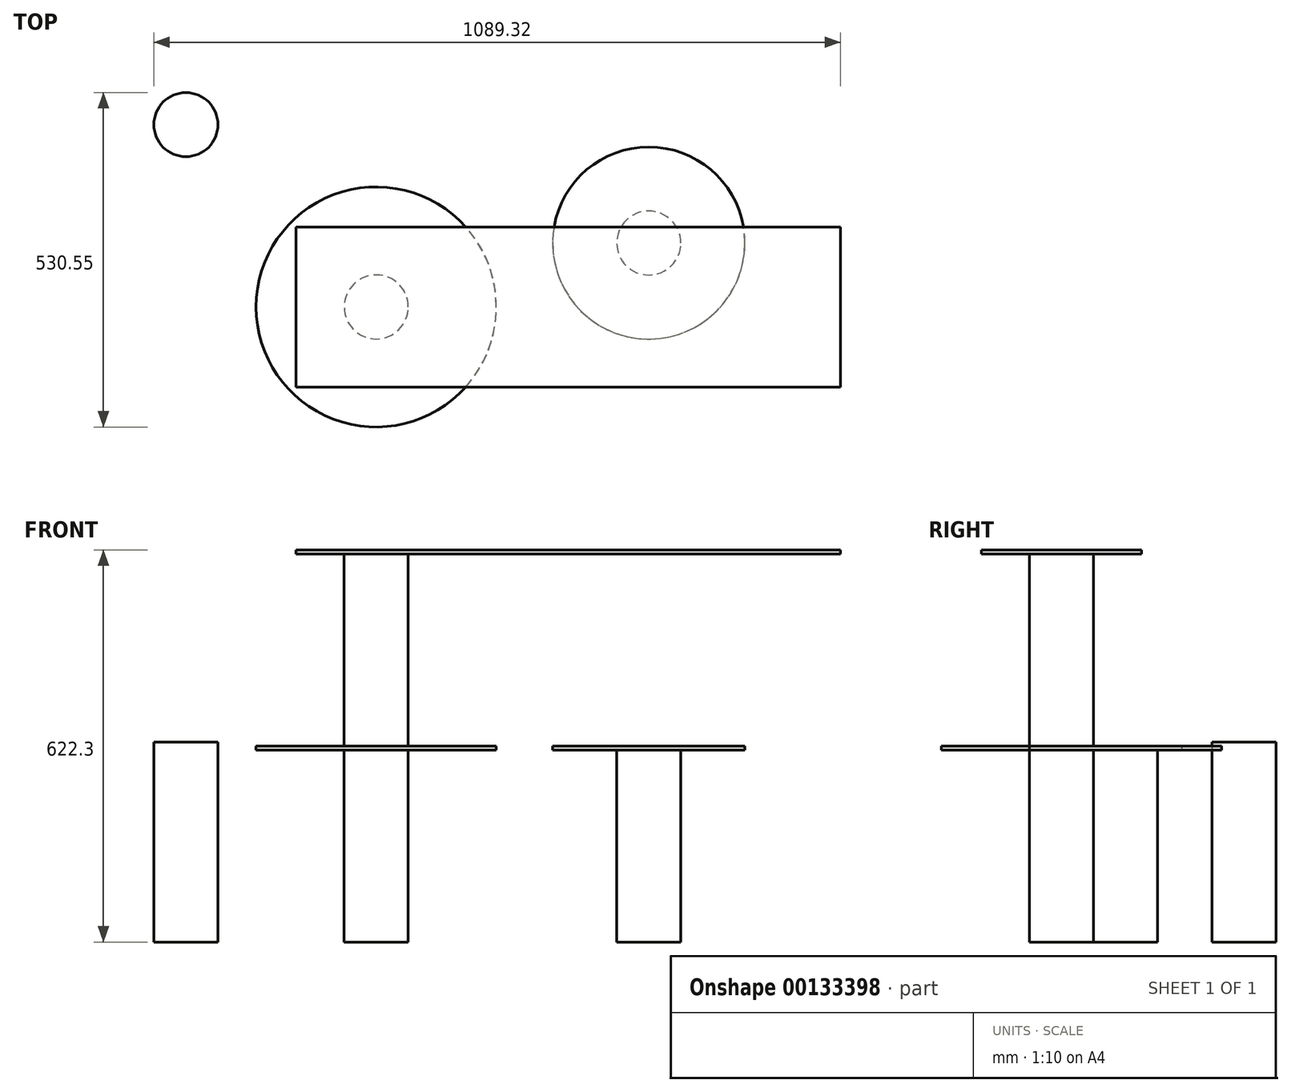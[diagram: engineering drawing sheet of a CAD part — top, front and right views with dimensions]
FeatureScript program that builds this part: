
annotation { "Feature Type Name" : "Feature", "Feature Type Description" : "" }
export const myFeature = defineFeature(function(context is Context, id is Id, definition is map)
    precondition{}
    {
        {
            var Q0;
            Q0=qCreatedBy(makeId("Top.planeOp"),FACE);
            var sketch = newSketch(context, id + "F0", { "sketchPlane" : qUnion([Q0])});
            skCircle(sketch, "E0", {"center": v(0, 0) * mm, "radius": 50.8 * mm});
            skSolve(sketch);
        }
        {
            var Q0;
            Q0 = qSketchRegion(id + "F0", true);
            extrude(context, id + "F1", {"entities" : qUnion([Q0]), "depth" : 304.8 * mm});
        }
        {
            var Q0;
            Q0=makeQuery(id+"F1.opExtrude","CAP_FACE",FACE,{"disambiguationData":[OSD([sQuery(id+"F0.wireOp",EDGE,"E0")])],"isStart":false});
            var sketch = newSketch(context, id + "F2", { "sketchPlane" : qUnion([Q0])});
            skCircle(sketch, "E1", {"center": v(0, 0) * mm, "radius": 152.4 * mm});
            skSolve(sketch);
        }
        {
            var Q0;
            Q0 = qSketchRegion(id + "F2", true);
            extrude(context, id + "F3", {"entities" : qUnion([Q0]), "operationType" : NewBodyOperationType.ADD, "depth" : 6.35 * mm});
        }
        {
            var Q0;
            Q0=qCreatedBy(makeId("Top.planeOp"),FACE);
            var sketch = newSketch(context, id + "F4", { "sketchPlane" : qUnion([Q0])});
            skCircle(sketch, "E2", {"center": v(-432.24, -101.35) * mm, "radius": 50.8 * mm});
            skSolve(sketch);
        }
        {
            var Q0;
            Q0 = qSketchRegion(id + "F4", true);
            extrude(context, id + "F5", {"entities" : qUnion([Q0]), "depth" : 304.8 * mm});
        }
        {
            var Q0;
            Q0=makeQuery(id+"F5.opExtrude","CAP_FACE",FACE,{"disambiguationData":[OSD([sQuery(id+"F4.wireOp",EDGE,"E2")])],"isStart":false});
            var sketch = newSketch(context, id + "F6", { "sketchPlane" : qUnion([Q0])});
            skCircle(sketch, "E3", {"center": v(-432.24, -101.35) * mm, "radius": 190.5 * mm});
            skSolve(sketch);
        }
        {
            var Q0;
            Q0 = qSketchRegion(id + "F6", true);
            extrude(context, id + "F7", {"entities" : qUnion([Q0]), "operationType" : NewBodyOperationType.ADD, "depth" : 6.35 * mm});
        }
        {
            var Q0;
            Q0=makeQuery(id+"F7.opExtrude","CAP_FACE",FACE,{"disambiguationData":[OSD([sQuery(id+"F6.wireOp",EDGE,"E3")])],"isStart":false});
            var sketch = newSketch(context, id + "F8", { "sketchPlane" : qUnion([Q0])});
            skCircle(sketch, "E4", {"center": v(-432.24, -101.35) * mm, "radius": 50.8 * mm});
            skSolve(sketch);
        }
        {
            var Q0;
            Q0 = qSketchRegion(id + "F8", true);
            extrude(context, id + "F9", {"entities" : qUnion([Q0]), "operationType" : NewBodyOperationType.ADD, "depth" : 304.8 * mm});
        }
        {
            var Q0;
            Q0=makeQuery(id+"F9.opExtrude","CAP_FACE",FACE,{"disambiguationData":[OSD([sQuery(id+"F8.wireOp",EDGE,"E4")])],"isStart":false});
            var sketch = newSketch(context, id + "F10", { "sketchPlane" : qUnion([Q0])});
            skLineSegment(sketch, "E5.bottom", {"start": v(-305.24, -228.35) * mm, "end": v(-559.24, -228.35) * mm});
            skLineSegment(sketch, "E5.top", {"start": v(-305.24, 25.65) * mm, "end": v(-559.24, 25.65) * mm});
            skLineSegment(sketch, "E5.left", {"start": v(-305.24, -228.35) * mm, "end": v(-305.24, 25.65) * mm});
            skLineSegment(sketch, "E5.right", {"start": v(-559.24, -228.35) * mm, "end": v(-559.24, 25.65) * mm});
            skPoint(sketch, "E5.middle", {"position": v(-432.24, -101.35) * mm});
            skSolve(sketch);
        }
        {
            var Q0;
            Q0 = qSketchRegion(id + "F10", true);
            extrude(context, id + "F11", {"entities" : qUnion([Q0]), "operationType" : NewBodyOperationType.ADD, "depth" : 6.35 * mm});
        }
        {
            var Q0;
            Q0=makeQuery(id+"F11.opExtrude","SWEPT_FACE",FACE,{"disambiguationData":[OSD([sQuery(id+"F10.wireOp",EDGE,"E5.left")])]});
            var sketch = newSketch(context, id + "F12", { "sketchPlane" : qUnion([Q0])});
            skLineSegment(sketch, "E6.bottom", {"start": v(-228.35, 615.95) * mm, "end": v(25.65, 615.95) * mm});
            skLineSegment(sketch, "E6.top", {"start": v(-228.35, 622.3) * mm, "end": v(25.65, 622.3) * mm});
            skLineSegment(sketch, "E6.left", {"start": v(-228.35, 615.95) * mm, "end": v(-228.35, 622.3) * mm});
            skLineSegment(sketch, "E6.right", {"start": v(25.65, 615.95) * mm, "end": v(25.65, 622.3) * mm});
            skSolve(sketch);
        }
        {
            var Q0;
            Q0 = qSketchRegion(id + "F12", true);
            extrude(context, id + "F13", {"entities" : qUnion([Q0]), "operationType" : NewBodyOperationType.ADD, "depth" : 609.6 * mm});
        }
        {
            var Q0;
            Q0=qCreatedBy(makeId("Top.planeOp"),FACE);
            var sketch = newSketch(context, id + "F14", { "sketchPlane" : qUnion([Q0])});
            skCircle(sketch, "E7", {"center": v(-734.16, 187.9) * mm, "radius": 50.8 * mm});
            skSolve(sketch);
        }
        {
            var Q0;
            Q0 = qSketchRegion(id + "F14", true);
            extrude(context, id + "F15", {"entities" : qUnion([Q0]), "depth" : 317.5 * mm});
        }
    });
